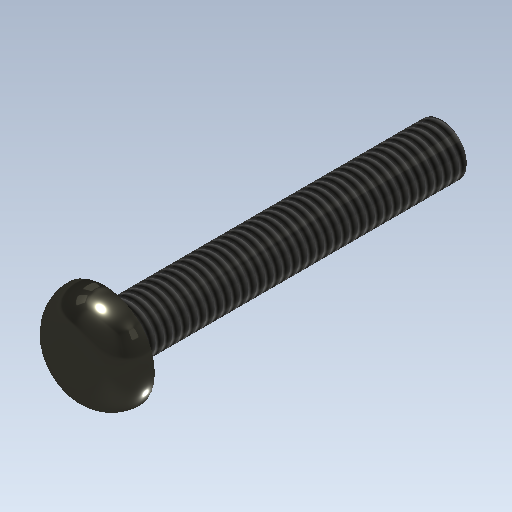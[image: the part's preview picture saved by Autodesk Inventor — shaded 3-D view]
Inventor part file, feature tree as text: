
AUTODESK INVENTOR PART (.ipt)
format: ipt  version: 2020.2 (Build 242310000, 310)  size: 166,912 bytes
history: native  units: mm
features: extrude x4, sketch x4, other x1, fillet x1, thread x1
ambient origin geometry x1: Origin
bodies: Body1 (feature_tree)
feature tree (11):
  other  "ソリッド1"
  extrude  "押し出し1"  Depth=3.0mm
  extrude  "押し出し2"  Depth=6.0mm TaperAngle=0.0deg
  fillet  "フィレット1"  Radius=6.0mm
  thread  "ねじ1"
  extrude  "押し出し3"  Depth=2.0mm TaperAngle=0.0deg
  extrude  "押し出し4"  Depth=2.0mm
  sketch  "スケッチ1"
  sketch  "スケッチ2"
  sketch  "スケッチ3"
  sketch  "スケッチ4"
